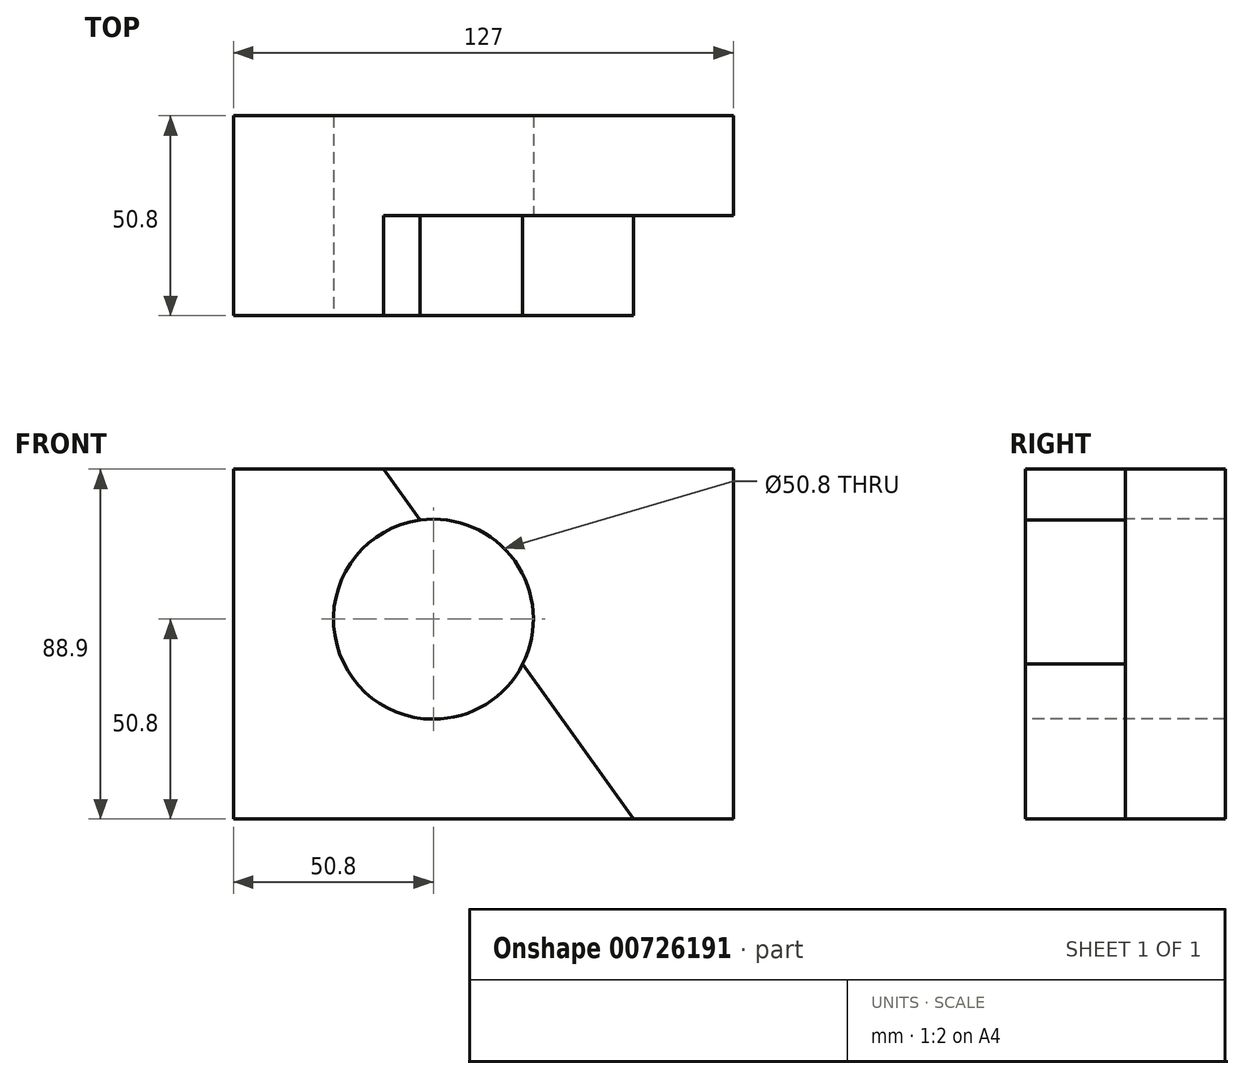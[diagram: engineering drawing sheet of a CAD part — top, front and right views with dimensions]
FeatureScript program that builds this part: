
annotation { "Feature Type Name" : "Feature", "Feature Type Description" : "" }
export const myFeature = defineFeature(function(context is Context, id is Id, definition is map)
    precondition{}
    {
        {
            var Q0;
            Q0=qCreatedBy(makeId("Front.planeOp"),FACE);
            var sketch = newSketch(context, id + "F0", { "sketchPlane" : qUnion([Q0])});
            skLineSegment(sketch, "E0.bottom", {"start": v(0, 0) * mm, "end": v(127, 0) * mm});
            skLineSegment(sketch, "E0.top", {"start": v(0, -88.9) * mm, "end": v(127, -88.9) * mm});
            skLineSegment(sketch, "E0.left", {"start": v(0, 0) * mm, "end": v(0, -88.9) * mm});
            skLineSegment(sketch, "E0.right", {"start": v(127, 0) * mm, "end": v(127, -88.9) * mm});
            skSolve(sketch);
        }
        {
            var Q0;
            Q0 = qSketchRegion(id + "F0", true);
            extrude(context, id + "F1", {"entities" : qUnion([Q0]), "depth" : 50.8 * mm, "offsetDistance" : 25.4 * mm});
        }
        {
            var Q0;
            Q0=makeQuery(id+"F1.opExtrude","CAP_FACE",FACE,{"disambiguationData":[OSD([sQuery(id+"F0.wireOp",EDGE,"E0.bottom"),sQuery(id+"F0.wireOp",EDGE,"E0.top"),sQuery(id+"F0.wireOp",EDGE,"E0.left"),sQuery(id+"F0.wireOp",EDGE,"E0.right")])],"isStart":false});
            var sketch = newSketch(context, id + "F2", { "sketchPlane" : qUnion([Q0])});
            skLineSegment(sketch, "E1", {"start": v(38.1, 0) * mm, "end": v(101.6, -88.9) * mm});
            skLineSegment(sketch, "E2", {"start": v(101.6, -88.9) * mm, "end": v(127, -88.9) * mm});
            skLineSegment(sketch, "E3", {"start": v(127, -88.9) * mm, "end": v(127, 0) * mm});
            skLineSegment(sketch, "E4", {"start": v(127, 0) * mm, "end": v(38.1, 0) * mm});
            skSolve(sketch);
        }
        {
            var Q0;
            Q0 = qSketchRegion(id + "F2", true);
            extrude(context, id + "F3", {"entities" : qUnion([Q0]), "operationType" : NewBodyOperationType.REMOVE, "oppositeDirection" : true, "depth" : 25.4 * mm, "offsetDistance" : 25.4 * mm});
        }
        {
            var Q0;
            Q0=makeQuery(id+"F1.opExtrude","CAP_FACE",FACE,{"disambiguationData":[OSD([sQuery(id+"F0.wireOp",EDGE,"E0.bottom"),sQuery(id+"F0.wireOp",EDGE,"E0.top"),sQuery(id+"F0.wireOp",EDGE,"E0.left"),sQuery(id+"F0.wireOp",EDGE,"E0.right")])],"isStart":false});
            var sketch = newSketch(context, id + "F4", { "sketchPlane" : qUnion([Q0])});
            skCircle(sketch, "E5", {"center": v(50.8, -38.1) * mm, "radius": 25.4 * mm});
            skSolve(sketch);
        }
        {
            var Q0;
            Q0 = qSketchRegion(id + "F4", true);
            extrude(context, id + "F5", {"entities" : qUnion([Q0]), "operationType" : NewBodyOperationType.REMOVE, "oppositeDirection" : true, "depth" : 50.8 * mm, "offsetDistance" : 25.4 * mm});
        }
    });
